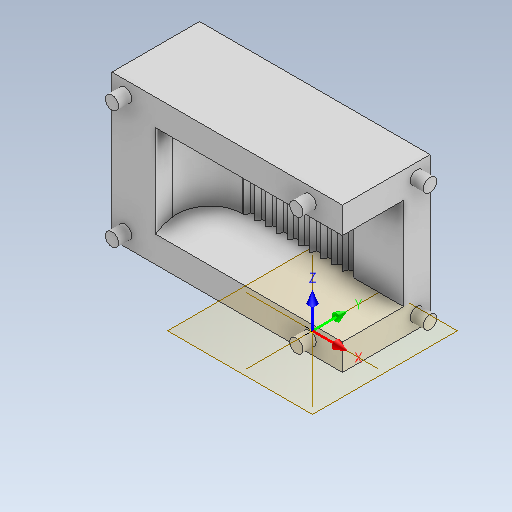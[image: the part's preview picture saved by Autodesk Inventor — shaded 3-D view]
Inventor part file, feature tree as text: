
AUTODESK INVENTOR PART (.ipt)
format: ipt  version: 2025.2 (Build 292293000, 293)  size: 508,416 bytes
history: native  units: mm
features: sketch x13, extrude x12, other x9, fillet x3, plane x1
ambient origin geometry x8: Origin, YZ Plane, XZ Plane, XY Plane, X Axis, Y Axis, Z Axis, Center Point
bodies: Volumenkörper2 (feature_tree), Volumenkörper3 (feature_tree)
feature tree (38):
  sketch  "Skizze1"  dims[d0=0.0mm d1=0.0mm d2=0.0mm d3=0.0mm d4=0.0mm d5=0.0mm d13=29.5mm d14=18.6mm d16=0.0mm d17=14.0mm]
  other  "BKS1"
  plane  "Arbeitsebene1"
  extrude  "Extrusion3"  Depth=14.0mm TaperAngle=0.0deg
  other  "Kombinieren1"
  extrude  "Extrusion9"  Depth=5.0mm
  extrude  "Extrusion10"  Depth=4.0mm
  extrude  "Extrusion11"  Depth=4.0mm
  extrude  "Extrusion12"  Depth=2.0mm TaperAngle=0.0deg
  extrude  "Extrusion13"  Depth=2.0mm TaperAngle=0.0deg
  extrude  "Extrusion14"  Depth=2.0mm
  extrude  "Extrusion15"  Depth=2.0mm
  extrude  "Extrusion16"  Depth=2.0mm
  extrude  "Extrusion17"  Depth=2.0mm
  extrude  "Extrusion18"  Depth=2.0mm
  fillet  "Rundung5"  Radius=2.0mm
  sketch  "Skizze22"  dims[d42=35.0mm d43=0.0mm d52=4.0mm]
  sketch  "Skizze29"  dims[d53=4.0mm d54=4.0mm]
  sketch  "Skizze30"  dims[d55=4.0mm d62=2.0mm d63=0.0mm]
  sketch  "Skizze31"  dims[d64=2.0mm d65=0.0mm d66=2.0mm d67=0.0mm]
  sketch  "Skizze32"  dims[d68=2.0mm d69=0.0mm d70=2.0mm]
  sketch  "Skizze33"  dims[d71=2.0mm d73=2.0mm]
  sketch  "Skizze34"  dims[d74=2.0mm d76=2.0mm]
  sketch  "Skizze35"  dims[d77=2.0mm d80=2.0mm]
  sketch  "Skizze36"  dims[d82=2.0mm d83=2.0mm d84=2.0mm]
  sketch  "Skizze37"  dims[d85=2.0mm d86=2.0mm d87=40.0mm d88=0.0mm d90=2.0mm d91=0.0mm]
  sketch  "Skizze42"  dims[d92=2.0mm d93=0.0mm d94=2.0mm d95=0.0mm d96=2.0mm d97=0.0mm d98=2.0mm d99=2.0mm d100=2.0mm d101=2.0mm d102=2.0mm d103=2.0mm d104=2.0mm d105=2.0mm d106=5.0mm d107=2.0mm d108=2.0mm d109=5.0mm d111=14.0mm d114=9.3mm d115=9.3mm d141=12.211865mm d142=12.211865mm d143=12.211865mm d146=0.0mm d147=14.0mm d148=0.0mm d149=0.5mm d110=0.5mm d112=0.5mm d113=0.872665mm]
  other  "BKS1: YZ-Ebene"
  other  "BKS1: XZ-Ebene"
  other  "BKS1: XY-Ebene"
  other  "BKS1: X-Achse"
  other  "BKS1: Y-Achse"
  other  "BKS1: Z-Achse"
  other  "BKS1: Mittelpunkt"
  sketch  "Skizze3"  dims[d18=15.0mm d19=5.0mm]
  extrude  "Extrusion2"  Depth=2.0mm
  fillet  "Rundung4"  Radius=40.0mm
  fillet  "Rundung3"  Radius=2.0mm
